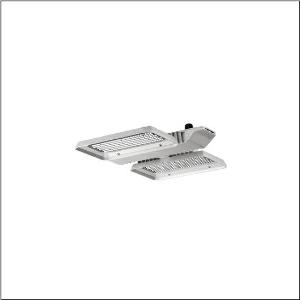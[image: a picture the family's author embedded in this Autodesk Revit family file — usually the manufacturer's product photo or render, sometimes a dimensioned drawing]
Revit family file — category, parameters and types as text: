
# Revit family: highbay_11_51hla2d14fca
name_source: partatom
category: Lighting Fixtures
units: mm (PartAtom-declared; Revit-internal decimal feet)

## family parameters
Cut with Voids When Loaded = No
Host = Face
Light Source = No
Part Type = Normal
Room Calculation Point = No
Round Connector Dimension = Use Diameter
Shared = No

## types (1)
- --- (1 x LED, 14400 lm, 81.2 W, 4000K)
    Apparent Load = 81 VA
    CIE Flux Codes = 89 96 99 100 100
    Color Rendering = 80
    Color Temperature = 4000K
    Default Elevation = 1800 mm
    Description = Highbay 11, LED high bay luminaire, primary light control with lens, of PMMA, light emission: direct distribution, primary light characteristic: symmetric, installation type: surface-mounted, suspended mounting, for 1x 2x LED, rated luminous flux: 14.400lm, luminous efficacy: 177lm/W, light colour: 840, colour temperature: 4000K, control gear: ECG DALI, with terminal, 5-pole, max. 2.5mm², mains connection: 230..240V, AC, 50/60Hz, rated input power: 81W, LED unit, of diecast aluminium, unplated, bead blasted, silver, length: 470mm, width: 500mm, height: 65mm, housing, of diecast aluminium, uncoated, bead blasted, silver, protection rating (complete): IP65, insulation class (complete): insulation class I (protective earthing), certification: CE, ENEC, VDE, UKCA, protection symbol: D, impact resistance: IK08 with glass or PC cover, permissible operating ambient temperature: -35..+55°C, reducing of maximum allowable ambient temperature of 5°C with ceiling mounting, corresponds to IFS (International Featured Standards) requirements for safety and quality in the food industry, packaging unit: 1 piece
    Height = 95 mm
    Lamp = 1 x LED
    Lamp Light Flux = 14400 lm
    Lamp Power = 81.2 W
    Lamp count = 1
    Length = 468 mm
    Luminous efficacy = 177 lm/W
    Manufacturer = Siteco
    ModVariant = No
    Model = 51HLA2D14FCA
    Mounting Place = Ceiling
    Mounting Type = Pendant
    Number of Poles = 1
    OnlyDefault = Yes
    Power Factor = 1
    Product Name = Highbay 11
    Product group = LED high bay luminaire
    ProductGroupID = 903
    Protection Class = Protection class I
    Protection Degree = IP 65
    RLX_Detail_Level = 1
    RLX_Emergency_Light_Flux = 0 lm
    RLX_Emergency_Type = 0
    RLX_Emergency_Type_DB = No
    RlxData = <blob elided: 86341 chars, md5=9cde3e89>
    Socket = socket
    Standby Power = 0 W
    System Light Flux = 14400 lm
    System Power = 81 W
    Type Comments = factory setting: luminous flux: 100 % | dim-lin: 254 | 460 mA
    Type Image = l_1003425.jpg
    URL = http://relux.com
    VarID = @adj_177439
    Voltage = 0 V
    Weight = 0.00 kg
    Width = 501 mm

## geometry (parser evidence)
native form markers: Blend x4, Sweep x11
no freeform markers — native parametric forms only
